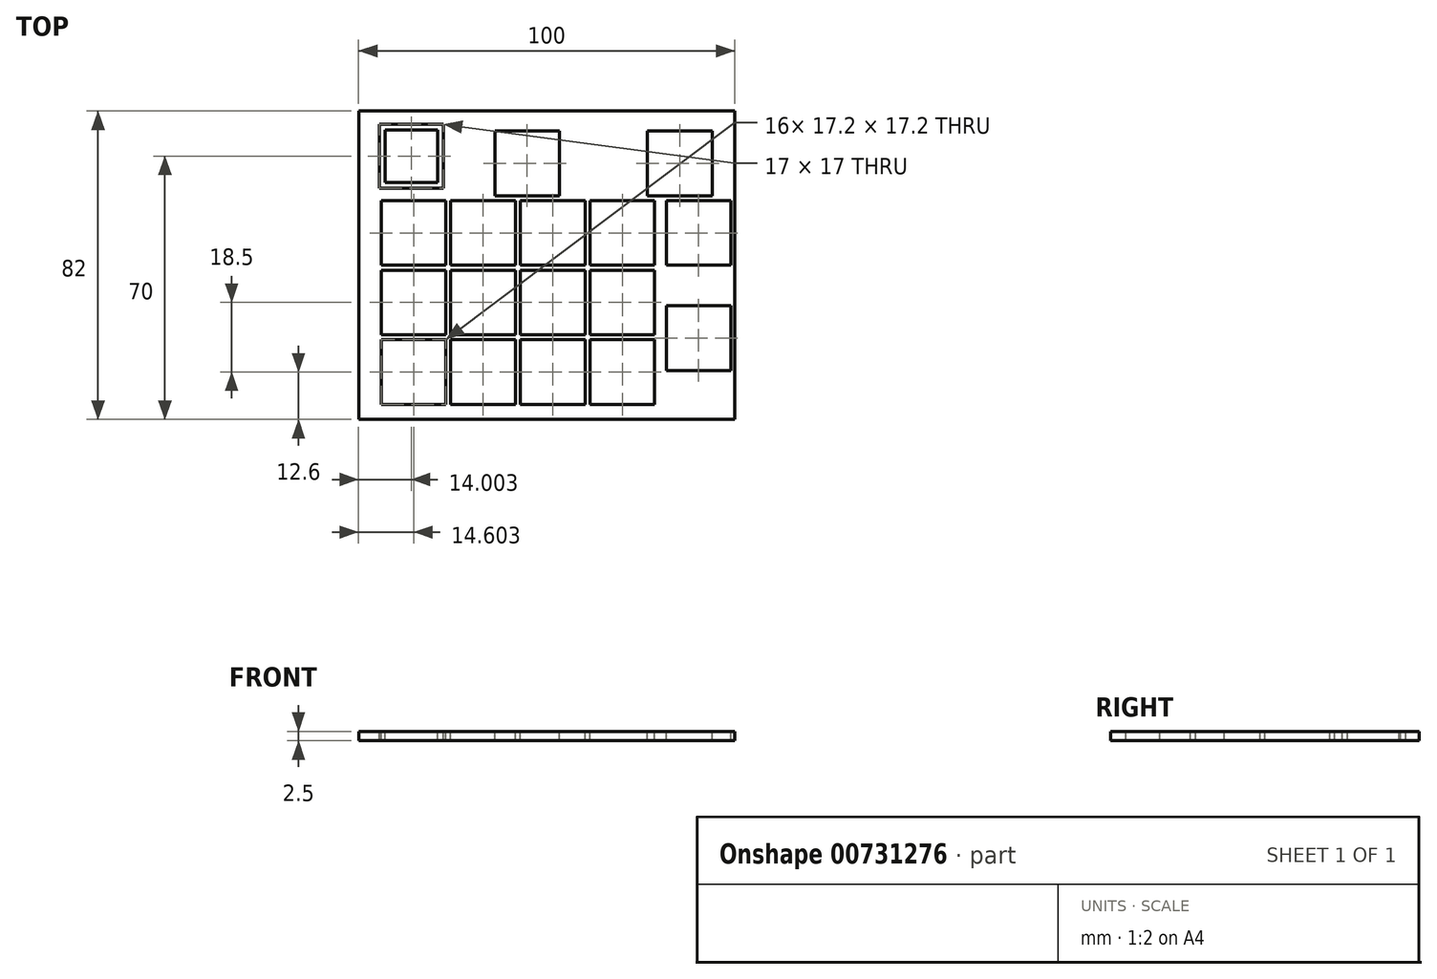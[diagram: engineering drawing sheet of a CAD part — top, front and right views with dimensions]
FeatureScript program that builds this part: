
annotation { "Feature Type Name" : "Feature", "Feature Type Description" : "" }
export const myFeature = defineFeature(function(context is Context, id is Id, definition is map)
    precondition{}
    {
        {
            var Q0;
            Q0=qCreatedBy(makeId("Top.planeOp"),FACE);
            var sketch = newSketch(context, id + "F0", { "sketchPlane" : qUnion([Q0])});
            skLineSegment(sketch, "E0.bottom", {"start": v(-89.14, 0) * mm, "end": v(10.86, 0) * mm});
            skLineSegment(sketch, "E0.top", {"start": v(-89.14, -82) * mm, "end": v(10.86, -82) * mm});
            skLineSegment(sketch, "E0.left", {"start": v(-89.14, 0) * mm, "end": v(-89.14, -82) * mm});
            skLineSegment(sketch, "E0.right", {"start": v(10.86, 0) * mm, "end": v(10.86, -82) * mm});
            skSolve(sketch);
        }
        {
            var Q0;
            Q0=makeQuery(id+"F0.imprint","IMPRINT",FACE,{"disambiguationData":[TD([[makeQuery(id+"F0.imprint","IMPRINT",EDGE,{"derivedFrom":sQuery(id+"F0.wireOp",EDGE,"E0.bottom")}),-1.0]])]});
            extrude(context, id + "F1", {"entities" : qUnion([Q0]), "depth" : 2.5 * mm, "offsetDistance" : 25 * mm});
        }
        {
            var Q0;
            Q0=makeQuery(id+"F1.opExtrude","CAP_FACE",FACE,{"disambiguationData":[OSD([sQuery(id+"F0.wireOp",EDGE,"E0.bottom"),sQuery(id+"F0.wireOp",EDGE,"E0.top"),sQuery(id+"F0.wireOp",EDGE,"E0.left"),sQuery(id+"F0.wireOp",EDGE,"E0.right")])],"isStart":false});
            var sketch = newSketch(context, id + "F2", { "sketchPlane" : qUnion([Q0])});
            skLineSegment(sketch, "E1.bottom", {"start": v(-83.14, -78) * mm, "end": v(-65.94, -78) * mm});
            skLineSegment(sketch, "E1.top", {"start": v(-83.14, -60.8) * mm, "end": v(-65.94, -60.8) * mm});
            skLineSegment(sketch, "E1.left", {"start": v(-83.14, -78) * mm, "end": v(-83.14, -60.8) * mm});
            skLineSegment(sketch, "E1.right", {"start": v(-65.94, -78) * mm, "end": v(-65.94, -60.8) * mm});
            skLineSegment(sketch, "E2.bottom", {"start": v(-65.94, -59.5) * mm, "end": v(-83.14, -59.5) * mm});
            skLineSegment(sketch, "E2.top", {"start": v(-65.94, -42.3) * mm, "end": v(-83.14, -42.3) * mm});
            skLineSegment(sketch, "E2.left", {"start": v(-65.94, -59.5) * mm, "end": v(-65.94, -42.3) * mm});
            skLineSegment(sketch, "E2.right", {"start": v(-83.14, -59.5) * mm, "end": v(-83.14, -42.3) * mm});
            skLineSegment(sketch, "E3.bottom", {"start": v(-65.94, -41) * mm, "end": v(-83.14, -41) * mm});
            skLineSegment(sketch, "E3.top", {"start": v(-65.94, -23.8) * mm, "end": v(-83.14, -23.8) * mm});
            skLineSegment(sketch, "E3.left", {"start": v(-65.94, -41) * mm, "end": v(-65.94, -23.8) * mm});
            skLineSegment(sketch, "E3.right", {"start": v(-83.14, -41) * mm, "end": v(-83.14, -23.8) * mm});
            skLineSegment(sketch, "E4.bottom", {"start": v(-82.14, -5) * mm, "end": v(-68.14, -5) * mm});
            skLineSegment(sketch, "E4.top", {"start": v(-82.14, -19) * mm, "end": v(-68.14, -19) * mm});
            skLineSegment(sketch, "E4.left", {"start": v(-82.14, -5) * mm, "end": v(-82.14, -19) * mm});
            skLineSegment(sketch, "E4.right", {"start": v(-68.14, -5) * mm, "end": v(-68.14, -19) * mm});
            skLineSegment(sketch, "E5.bottom", {"start": v(-83.64, -3.5) * mm, "end": v(-66.64, -3.5) * mm});
            skLineSegment(sketch, "E5.top", {"start": v(-83.64, -20.5) * mm, "end": v(-66.64, -20.5) * mm});
            skLineSegment(sketch, "E5.left", {"start": v(-83.64, -3.5) * mm, "end": v(-83.64, -20.5) * mm});
            skLineSegment(sketch, "E5.right", {"start": v(-66.64, -3.5) * mm, "end": v(-66.64, -20.5) * mm});
            skSolve(sketch);
        }
        {
            var Q0;
            Q0=makeQuery(id+"F2.imprint","IMPRINT",FACE,{"disambiguationData":[TD([[makeQuery(id+"F2.imprint","IMPRINT",EDGE,{"derivedFrom":sQuery(id+"F2.wireOp",EDGE,"E1.bottom")}),1.0]])]});
            extrude(context, id + "F3", {"entities" : qUnion([Q0]), "operationType" : NewBodyOperationType.REMOVE, "oppositeDirection" : true, "depth" : 25 * mm, "offsetDistance" : 25 * mm});
        }
        {
            var Q0;
            Q0=qSketchRegion(id+"F2",true);
            extrude(context, id + "F4", {"entities" : qUnion([Q0]), "operationType" : NewBodyOperationType.REMOVE, "oppositeDirection" : true, "depth" : 25 * mm, "offsetDistance" : 25 * mm});
        }
        {
            var Q0;
            Q0=makeQuery(id+"F1.opExtrude","CAP_FACE",FACE,{"disambiguationData":[OSD([sQuery(id+"F0.wireOp",EDGE,"E0.bottom"),sQuery(id+"F0.wireOp",EDGE,"E0.top"),sQuery(id+"F0.wireOp",EDGE,"E0.left"),sQuery(id+"F0.wireOp",EDGE,"E0.right")])],"isStart":false});
            var sketch = newSketch(context, id + "F5", { "sketchPlane" : qUnion([Q0])});
            skLineSegment(sketch, "E6.bottom", {"start": v(-64.64, -78) * mm, "end": v(-47.44, -78) * mm});
            skLineSegment(sketch, "E6.top", {"start": v(-64.64, -60.8) * mm, "end": v(-47.44, -60.8) * mm});
            skLineSegment(sketch, "E6.left", {"start": v(-64.64, -78) * mm, "end": v(-64.64, -60.8) * mm});
            skLineSegment(sketch, "E6.right", {"start": v(-47.44, -78) * mm, "end": v(-47.44, -60.8) * mm});
            skLineSegment(sketch, "E7.bottom", {"start": v(-46.14, -78) * mm, "end": v(-28.94, -78) * mm});
            skLineSegment(sketch, "E7.top", {"start": v(-46.14, -60.8) * mm, "end": v(-28.94, -60.8) * mm});
            skLineSegment(sketch, "E7.left", {"start": v(-46.14, -78) * mm, "end": v(-46.14, -60.8) * mm});
            skLineSegment(sketch, "E7.right", {"start": v(-28.94, -78) * mm, "end": v(-28.94, -60.8) * mm});
            skLineSegment(sketch, "E8.bottom", {"start": v(-27.64, -78) * mm, "end": v(-10.44, -78) * mm});
            skLineSegment(sketch, "E8.top", {"start": v(-27.64, -60.8) * mm, "end": v(-10.44, -60.8) * mm});
            skLineSegment(sketch, "E8.left", {"start": v(-27.64, -78) * mm, "end": v(-27.64, -60.8) * mm});
            skLineSegment(sketch, "E8.right", {"start": v(-10.44, -78) * mm, "end": v(-10.44, -60.8) * mm});
            skSolve(sketch);
        }
        {
            var Q0;
            Q0=qSketchRegion(id+"F5",true);
            extrude(context, id + "F6", {"entities" : qUnion([Q0]), "operationType" : NewBodyOperationType.REMOVE, "oppositeDirection" : true, "depth" : 25 * mm, "offsetDistance" : 25 * mm});
        }
        {
            var Q0;
            Q0=makeQuery(id+"F1.opExtrude","CAP_FACE",FACE,{"disambiguationData":[OSD([sQuery(id+"F0.wireOp",EDGE,"E0.bottom"),sQuery(id+"F0.wireOp",EDGE,"E0.top"),sQuery(id+"F0.wireOp",EDGE,"E0.left"),sQuery(id+"F0.wireOp",EDGE,"E0.right")])],"isStart":false});
            var sketch = newSketch(context, id + "F7", { "sketchPlane" : qUnion([Q0])});
            skLineSegment(sketch, "E9.bottom", {"start": v(-47.44, -59.5) * mm, "end": v(-64.64, -59.5) * mm});
            skLineSegment(sketch, "E9.top", {"start": v(-47.44, -42.3) * mm, "end": v(-64.64, -42.3) * mm});
            skLineSegment(sketch, "E9.left", {"start": v(-47.44, -59.5) * mm, "end": v(-47.44, -42.3) * mm});
            skLineSegment(sketch, "E9.right", {"start": v(-64.64, -59.5) * mm, "end": v(-64.64, -42.3) * mm});
            skLineSegment(sketch, "E10.bottom", {"start": v(-47.44, -41) * mm, "end": v(-64.64, -41) * mm});
            skLineSegment(sketch, "E10.top", {"start": v(-47.44, -23.8) * mm, "end": v(-64.64, -23.8) * mm});
            skLineSegment(sketch, "E10.left", {"start": v(-47.44, -41) * mm, "end": v(-47.44, -23.8) * mm});
            skLineSegment(sketch, "E10.right", {"start": v(-64.64, -41) * mm, "end": v(-64.64, -23.8) * mm});
            skPoint(sketch, "E11.firstSnap0", {"position": v(-47.44, -32.4) * mm});
            skLineSegment(sketch, "E12.bottom", {"start": v(-28.94, -59.5) * mm, "end": v(-46.14, -59.5) * mm});
            skLineSegment(sketch, "E12.top", {"start": v(-28.94, -42.3) * mm, "end": v(-46.14, -42.3) * mm});
            skLineSegment(sketch, "E12.left", {"start": v(-28.94, -59.5) * mm, "end": v(-28.94, -42.3) * mm});
            skLineSegment(sketch, "E12.right", {"start": v(-46.14, -59.5) * mm, "end": v(-46.14, -42.3) * mm});
            skLineSegment(sketch, "E13.bottom", {"start": v(-28.94, -41) * mm, "end": v(-46.14, -41) * mm});
            skLineSegment(sketch, "E13.top", {"start": v(-28.94, -23.8) * mm, "end": v(-46.14, -23.8) * mm});
            skLineSegment(sketch, "E13.left", {"start": v(-28.94, -41) * mm, "end": v(-28.94, -23.8) * mm});
            skLineSegment(sketch, "E13.right", {"start": v(-46.14, -41) * mm, "end": v(-46.14, -23.8) * mm});
            skSolve(sketch);
        }
        {
            var Q0;
            Q0=qSketchRegion(id+"F7",true);
            extrude(context, id + "F8", {"entities" : qUnion([Q0]), "operationType" : NewBodyOperationType.REMOVE, "oppositeDirection" : true, "depth" : 25 * mm, "offsetDistance" : 25 * mm});
        }
        {
            var Q0;
            Q0=makeQuery(id+"F1.opExtrude","CAP_FACE",FACE,{"disambiguationData":[OSD([sQuery(id+"F0.wireOp",EDGE,"E0.bottom"),sQuery(id+"F0.wireOp",EDGE,"E0.top"),sQuery(id+"F0.wireOp",EDGE,"E0.left"),sQuery(id+"F0.wireOp",EDGE,"E0.right")])],"isStart":false});
            var sketch = newSketch(context, id + "F9", { "sketchPlane" : qUnion([Q0])});
            skLineSegment(sketch, "E14.bottom", {"start": v(-27.64, -59.5) * mm, "end": v(-10.44, -59.5) * mm});
            skLineSegment(sketch, "E14.top", {"start": v(-27.64, -42.3) * mm, "end": v(-10.44, -42.3) * mm});
            skLineSegment(sketch, "E14.left", {"start": v(-27.64, -59.5) * mm, "end": v(-27.64, -42.3) * mm});
            skLineSegment(sketch, "E14.right", {"start": v(-10.44, -59.5) * mm, "end": v(-10.44, -42.3) * mm});
            skLineSegment(sketch, "E15.bottom", {"start": v(-27.64, -41) * mm, "end": v(-10.44, -41) * mm});
            skLineSegment(sketch, "E15.top", {"start": v(-27.64, -23.8) * mm, "end": v(-10.44, -23.8) * mm});
            skLineSegment(sketch, "E15.left", {"start": v(-27.64, -41) * mm, "end": v(-27.64, -23.8) * mm});
            skLineSegment(sketch, "E15.right", {"start": v(-10.44, -41) * mm, "end": v(-10.44, -23.8) * mm});
            skSolve(sketch);
        }
        {
            var Q0;
            Q0=qSketchRegion(id+"F9",true);
            extrude(context, id + "F10", {"entities" : qUnion([Q0]), "operationType" : NewBodyOperationType.REMOVE, "oppositeDirection" : true, "depth" : 25 * mm, "offsetDistance" : 25 * mm});
        }
        {
            var Q0;
            Q0=makeQuery(id+"F1.opExtrude","CAP_FACE",FACE,{"disambiguationData":[OSD([sQuery(id+"F0.wireOp",EDGE,"E0.bottom"),sQuery(id+"F0.wireOp",EDGE,"E0.top"),sQuery(id+"F0.wireOp",EDGE,"E0.left"),sQuery(id+"F0.wireOp",EDGE,"E0.right")])],"isStart":false});
            var sketch = newSketch(context, id + "F11", { "sketchPlane" : qUnion([Q0])});
            skLineSegment(sketch, "E16.bottom", {"start": v(-7.34, -69) * mm, "end": v(9.86, -69) * mm});
            skLineSegment(sketch, "E16.top", {"start": v(-7.34, -51.8) * mm, "end": v(9.86, -51.8) * mm});
            skLineSegment(sketch, "E16.left", {"start": v(-7.34, -69) * mm, "end": v(-7.34, -51.8) * mm});
            skLineSegment(sketch, "E16.right", {"start": v(9.86, -69) * mm, "end": v(9.86, -51.8) * mm});
            skLineSegment(sketch, "E17.bottom", {"start": v(-7.34, -41) * mm, "end": v(9.86, -41) * mm});
            skLineSegment(sketch, "E17.top", {"start": v(-7.34, -23.8) * mm, "end": v(9.86, -23.8) * mm});
            skLineSegment(sketch, "E17.left", {"start": v(-7.34, -41) * mm, "end": v(-7.34, -23.8) * mm});
            skLineSegment(sketch, "E17.right", {"start": v(9.86, -41) * mm, "end": v(9.86, -23.8) * mm});
            skSolve(sketch);
        }
        {
            var Q0;
            Q0=qSketchRegion(id+"F11",true);
            extrude(context, id + "F12", {"entities" : qUnion([Q0]), "operationType" : NewBodyOperationType.REMOVE, "oppositeDirection" : true, "depth" : 25 * mm, "offsetDistance" : 25 * mm});
        }
        {
            var Q0;
            Q0=makeQuery(id+"F1.opExtrude","CAP_FACE",FACE,{"disambiguationData":[OSD([sQuery(id+"F0.wireOp",EDGE,"E0.bottom"),sQuery(id+"F0.wireOp",EDGE,"E0.top"),sQuery(id+"F0.wireOp",EDGE,"E0.left"),sQuery(id+"F0.wireOp",EDGE,"E0.right")])],"isStart":false});
            var sketch = newSketch(context, id + "F13", { "sketchPlane" : qUnion([Q0])});
            skLineSegment(sketch, "E18.bottom", {"start": v(-52.94, -22.5) * mm, "end": v(-35.74, -22.5) * mm});
            skLineSegment(sketch, "E18.top", {"start": v(-52.94, -5.3) * mm, "end": v(-35.74, -5.3) * mm});
            skLineSegment(sketch, "E18.left", {"start": v(-52.94, -22.5) * mm, "end": v(-52.94, -5.3) * mm});
            skLineSegment(sketch, "E18.right", {"start": v(-35.74, -22.5) * mm, "end": v(-35.74, -5.3) * mm});
            skSolve(sketch);
        }
        {
            var Q0;
            Q0=qSketchRegion(id+"F13",true);
            extrude(context, id + "F14", {"entities" : qUnion([Q0]), "operationType" : NewBodyOperationType.REMOVE, "oppositeDirection" : true, "depth" : 25 * mm, "offsetDistance" : 25 * mm});
        }
        {
            var Q0;
            Q0=makeQuery(id+"F1.opExtrude","CAP_FACE",FACE,{"disambiguationData":[OSD([sQuery(id+"F0.wireOp",EDGE,"E0.bottom"),sQuery(id+"F0.wireOp",EDGE,"E0.top"),sQuery(id+"F0.wireOp",EDGE,"E0.left"),sQuery(id+"F0.wireOp",EDGE,"E0.right")])],"isStart":false});
            var sketch = newSketch(context, id + "F15", { "sketchPlane" : qUnion([Q0])});
            skLineSegment(sketch, "E19.bottom", {"start": v(-12.34, -22.5) * mm, "end": v(4.86, -22.5) * mm});
            skLineSegment(sketch, "E19.top", {"start": v(-12.34, -5.3) * mm, "end": v(4.86, -5.3) * mm});
            skLineSegment(sketch, "E19.left", {"start": v(-12.34, -22.5) * mm, "end": v(-12.34, -5.3) * mm});
            skLineSegment(sketch, "E19.right", {"start": v(4.86, -22.5) * mm, "end": v(4.86, -5.3) * mm});
            skSolve(sketch);
        }
        {
            var Q0;
            Q0=qSketchRegion(id+"F15",true);
            extrude(context, id + "F16", {"entities" : qUnion([Q0]), "operationType" : NewBodyOperationType.REMOVE, "oppositeDirection" : true, "depth" : 25 * mm, "offsetDistance" : 25 * mm});
        }
    });
